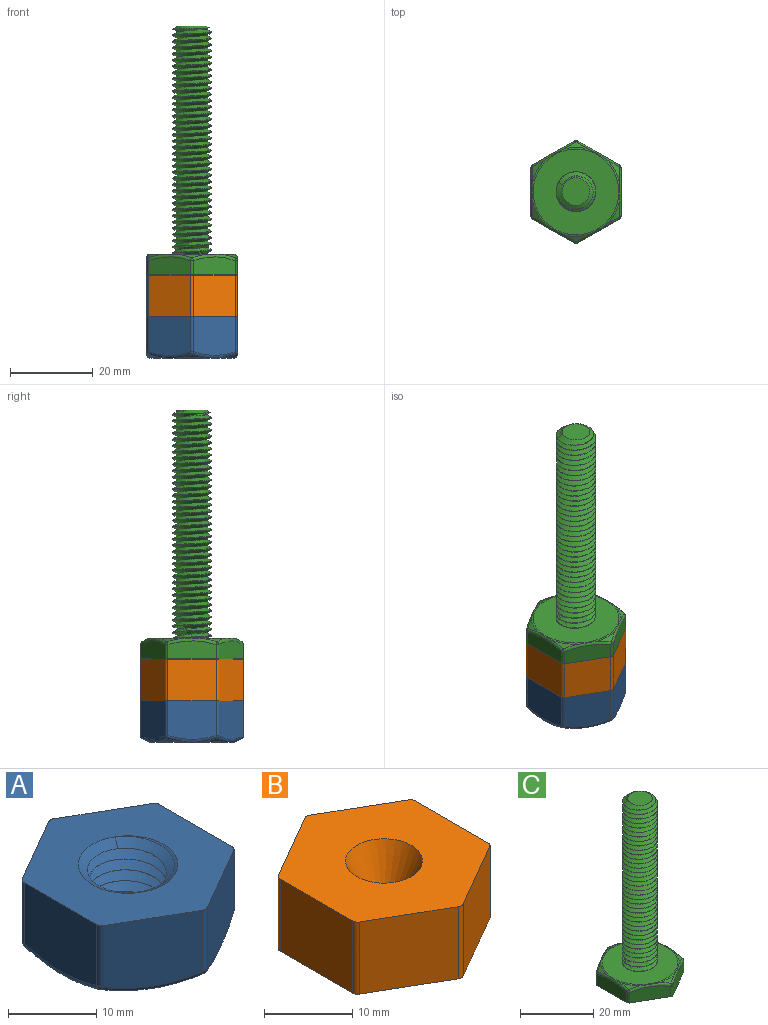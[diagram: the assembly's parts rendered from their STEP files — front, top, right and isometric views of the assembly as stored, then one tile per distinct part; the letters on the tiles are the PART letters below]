
ASSEMBLY  parts=3 mates=2
PART A: 38 faces, bbox 23.6x24.8x11.5 mm
  f0: cone r=17.18mm half-angle=60deg, axis (0,0,1), area 4.7mm2, adj f26,f30,f33
  f1: cone r=17.18mm half-angle=60deg, axis (0,0,1), area 4.7mm2, adj f29,f30,f33
  f2: cone r=17.18mm half-angle=60deg, axis (0,0,1), area 4.7mm2, adj f23,f29,f30
  f3: cone r=17.18mm half-angle=60deg, axis (0,0,1), area 4.7mm2, adj f23,f24,f30
  f4: cone r=17.18mm half-angle=60deg, axis (0,0,1), area 4.7mm2, adj f24,f25,f30
  f5: plane 20.67x20.67mm, normal (0,0,-1), area 235.3mm2, adj f30,f34
  f6: plane 11.62x9.37mm, normal (-1,0,0), area 105.1mm2, adj f13,f27,f28,f33
  f7: plane 10.08x9.37mm, normal (-0.5,-0.87,0), area 105.1mm2, adj f13,f18,f28,f29
  f8: plane 10.08x9.37mm, normal (0.5,-0.87,0), area 105.1mm2, adj f13,f15,f18,f23
  f9: plane 11.61x9.37mm, normal (1,0,0), area 105.1mm2, adj f13,f15,f16,f24
  f10: plane 10.08x9.37mm, normal (0.5,0.87,0), area 105.1mm2, adj f13,f16,f17,f25
  f11: cylinder r=4.35mm len=8.7mm, axis (0,0,-1), area 2.1mm2, adj f34,f35,f36,f37
  f12: plane 10.08x9.37mm, normal (-0.5,0.87,0), area 105.1mm2, adj f13,f17,f26,f27
  f13: plane 24.81x21.7mm, normal (0,0,1), area 307.3mm2, adj f6,f7,f8,f9,f10,f12,f15,f16
  f14: cone r=17.18mm half-angle=60deg, axis (0,0,1), area 4.7mm2, adj f25,f26,f30
  f15: cylinder r=0.8mm len=8.47mm, axis (0,0,-1), area 7.1mm2, adj f8,f9,f13,f19
  f16: cylinder r=0.8mm len=8.47mm, axis (0,0,-1), area 7.1mm2, adj f9,f10,f13,f20
  f17: cylinder r=0.8mm len=8.47mm, axis (0,0,-1), area 7.1mm2, adj f10,f12,f13,f21
  f18: cylinder r=0.8mm len=8.47mm, axis (0,0,-1), area 7.1mm2, adj f7,f8,f13,f22
  f19: sphere r=0.8mm, area 0.4mm2, adj f15,f23,f24
  f20: sphere r=0.8mm, area 0.3mm2, adj f16,f24,f25
  f21: sphere r=0.8mm, area 0.3mm2, adj f17,f25,f26
  f22: sphere r=0.8mm, area 0.3mm2, adj f18,f23,f29
  f23: bspline ~10.49x6.3mm, area 10.3mm2, adj f2,f3,f8,f19,f22,f30
  f24: bspline ~16.37x2.28mm, area 9.9mm2, adj f3,f4,f9,f19,f20,f30
  f25: bspline ~10.49x6.3mm, area 10.3mm2, adj f4,f10,f14,f20,f21,f30
  f26: bspline ~10.49x6.3mm, area 10.3mm2, adj f0,f12,f14,f21,f30,f31
  f27: cylinder r=0.8mm len=8.47mm, axis (0,0,-1), area 7.1mm2, adj f6,f12,f13,f31
  f28: cylinder r=0.8mm len=8.47mm, axis (0,0,-1), area 7.1mm2, adj f6,f7,f13,f32
  f29: bspline ~10.49x6.3mm, area 10.3mm2, adj f1,f2,f7,f22,f30,f32
  f30: torus R=10.34mm, axis (0,0,1), area 24.5mm2, adj f0,f1,f2,f3,f4,f5,f14,f23
  f31: sphere r=0.8mm, area 0.3mm2, adj f26,f27,f33
  f32: sphere r=0.8mm, area 0.3mm2, adj f28,f29,f33
  f33: bspline ~12x1.59mm, area 10.3mm2, adj f0,f1,f6,f30,f31,f32
  f34: cone r=5.65mm half-angle=60deg, axis (0,0,-1), area 24.9mm2, adj f5,f11,f36,f37
  f35: cone r=4.35mm half-angle=60deg, axis (0,0,1), area 24.9mm2, adj f11,f13,f36,f37
  f36: bspline ~13.03x11.28mm, area 289.3mm2, adj f11,f34,f35,f37
  f37: bspline ~13.03x11.28mm, area 285mm2, adj f11,f34,f35,f36
PART B: 15 faces, bbox 21.7x24.8x10 mm
  f0: plane 11.6x10mm, normal (-1,0,0), area 116mm2, adj f7,f8,f9,f14
  f1: plane 10.05x10mm, normal (-0.5,-0.87,0), area 116mm2, adj f7,f8,f9,f10
  f2: plane 10.05x10mm, normal (0.5,-0.87,0), area 116mm2, adj f7,f8,f10,f11
  f3: plane 11.6x10mm, normal (1,0,0), area 116mm2, adj f7,f8,f11,f12
  f4: plane 10.05x10mm, normal (0.5,0.87,0), area 116mm2, adj f7,f8,f12,f13
  f5: cone r=4.35mm half-angle=25deg, axis (0,0,1), area 140.7mm2, adj f7
  f6: plane 10.05x10mm, normal (-0.5,0.87,0), area 116mm2, adj f7,f8,f13,f14
  f7: plane 24.81x21.7mm, normal (0,0,1), area 348.1mm2, adj f0,f1,f2,f3,f4,f5,f6,f9
  f8: plane 24.81x21.7mm, normal (0,0,-1), area 407.6mm2, adj f0,f1,f2,f3,f4,f6,f9,f10
  f9: cylinder r=0.8mm len=10mm, axis (0,0,-1), area 8.4mm2, adj f0,f1,f7,f8
  f10: cylinder r=0.8mm len=10mm, axis (0,0,-1), area 8.4mm2, adj f1,f2,f7,f8
  f11: cylinder r=0.8mm len=10mm, axis (0,0,-1), area 8.4mm2, adj f2,f3,f7,f8
  f12: cylinder r=0.8mm len=10mm, axis (0,0,-1), area 8.4mm2, adj f3,f4,f7,f8
  f13: cylinder r=0.8mm len=10mm, axis (0,0,-1), area 8.4mm2, adj f4,f6,f7,f8
  f14: cylinder r=0.8mm len=10mm, axis (0,0,-1), area 8.4mm2, adj f0,f6,f7,f8
PART C: 38 faces, bbox 24.5x25.7x61.6 mm
  f0: cone r=14.85mm half-angle=60deg, axis (0,0,-1), area 4.7mm2, adj f27,f33,f34
  f1: cone r=14.85mm half-angle=60deg, axis (0,0,-1), area 4.7mm2, adj f27,f28,f34
  f2: cone r=14.85mm half-angle=60deg, axis (0,0,-1), area 4.7mm2, adj f28,f29,f34
  f3: cone r=14.85mm half-angle=60deg, axis (0,0,-1), area 4.7mm2, adj f29,f30,f34
  f4: cone r=14.85mm half-angle=60deg, axis (0,0,-1), area 4.7mm2, adj f30,f34,f37
  f5: plane 21.59x21.59mm, normal (0,0,1), area 279.8mm2, adj f6,f7,f8,f34
  f6: cylinder r=4.75mm len=54.19mm, axis (0,0,-1), area -657mm2, adj f5,f7,f8,f10
  f7: bspline ~56.44x10.97mm, area 1313.4mm2, adj f5,f6,f8,f10
  f8: bspline ~55.69x10.97mm, area 1310.9mm2, adj f5,f6,f7,f10
  f9: plane 6.7x6.7mm, normal (0,0,1), area 35.3mm2, adj f10
  f10: cone r=3.35mm half-angle=60deg, axis (0,0,-1), area 23.7mm2, adj f6,f7,f8,f9
  f11: cone r=14.85mm half-angle=60deg, axis (0,0,-1), area 4.7mm2, adj f33,f34,f37
  f12: plane 24.81x21.7mm, normal (0,0,-1), area 407.6mm2, adj f13,f14,f15,f16,f17,f18,f19,f20
  f13: plane 10.08x5.83mm, normal (0.5,-0.87,0), area 47.1mm2, adj f12,f22,f32,f33
  f14: plane 10.08x5.83mm, normal (-0.5,-0.87,0), area 47.1mm2, adj f12,f19,f22,f27
  f15: plane 11.62x4.37mm, normal (-1,0,0), area 47.1mm2, adj f12,f19,f20,f28
  f16: plane 10.08x5.83mm, normal (-0.5,0.87,0), area 47.1mm2, adj f12,f20,f21,f29
  f17: plane 10.08x5.83mm, normal (0.5,0.87,0), area 47.1mm2, adj f12,f21,f30,f31
  f18: plane 11.62x4.37mm, normal (1,0,0), area 47.1mm2, adj f12,f31,f32,f37
  f19: cylinder r=0.8mm len=3.47mm, axis (0,0,-1), area 2.9mm2, adj f12,f14,f15,f23
  f20: cylinder r=0.8mm len=3.47mm, axis (0,0,-1), area 2.9mm2, adj f12,f15,f16,f24
  f21: cylinder r=0.8mm len=3.47mm, axis (0,0,-1), area 2.9mm2, adj f12,f16,f17,f25
  f22: cylinder r=0.8mm len=3.47mm, axis (0,0,-1), area 2.9mm2, adj f12,f13,f14,f26
  f23: sphere r=0.8mm, area 0.3mm2, adj f19,f27,f28
  f24: sphere r=0.8mm, area 0.3mm2, adj f20,f28,f29
  f25: sphere r=0.8mm, area 0.3mm2, adj f21,f29,f30
  f26: sphere r=0.8mm, area 0.3mm2, adj f22,f27,f33
  f27: bspline ~10.49x6.3mm, area 10.3mm2, adj f0,f1,f14,f23,f26,f34
  f28: bspline ~12x1.59mm, area 10.3mm2, adj f1,f2,f15,f23,f24,f34
  f29: bspline ~10.49x6.3mm, area 10.3mm2, adj f2,f3,f16,f24,f25,f34
  f30: bspline ~10.49x6.3mm, area 10.3mm2, adj f3,f4,f17,f25,f34,f35
  f31: cylinder r=0.8mm len=3.47mm, axis (0,0,-1), area 2.9mm2, adj f12,f17,f18,f35
  f32: cylinder r=0.8mm len=3.47mm, axis (0,0,-1), area 2.9mm2, adj f12,f13,f18,f36
  f33: bspline ~10.49x6.3mm, area 10.3mm2, adj f0,f11,f13,f26,f34,f36
  f34: torus R=10.34mm, axis (0,0,1), area 24.5mm2, adj f0,f1,f2,f3,f4,f5,f11,f27
  f35: sphere r=0.8mm, area 0.3mm2, adj f30,f31,f37
  f36: sphere r=0.8mm, area 0.3mm2, adj f32,f33,f37
  f37: bspline ~15.45x2.15mm, area 9.9mm2, adj f4,f11,f18,f34,f35,f36
PLACE A t=(-4.43,-5.53,-31.17)mm
PLACE B rot(axis=(1,0,0),180deg) t=(-4.43,-5.53,-21.17)mm
PLACE C t=(-4.43,-5.53,-16.17)mm
MATE fastened C.f6 <-> B.f5  axis (0,0,-1) through (-4.43,-5.53,-16.17)mm
MATE fastened B.f7 <-> A.f13  axis (0,0,-1) through (-9.85,3.87,-26.17)mm
